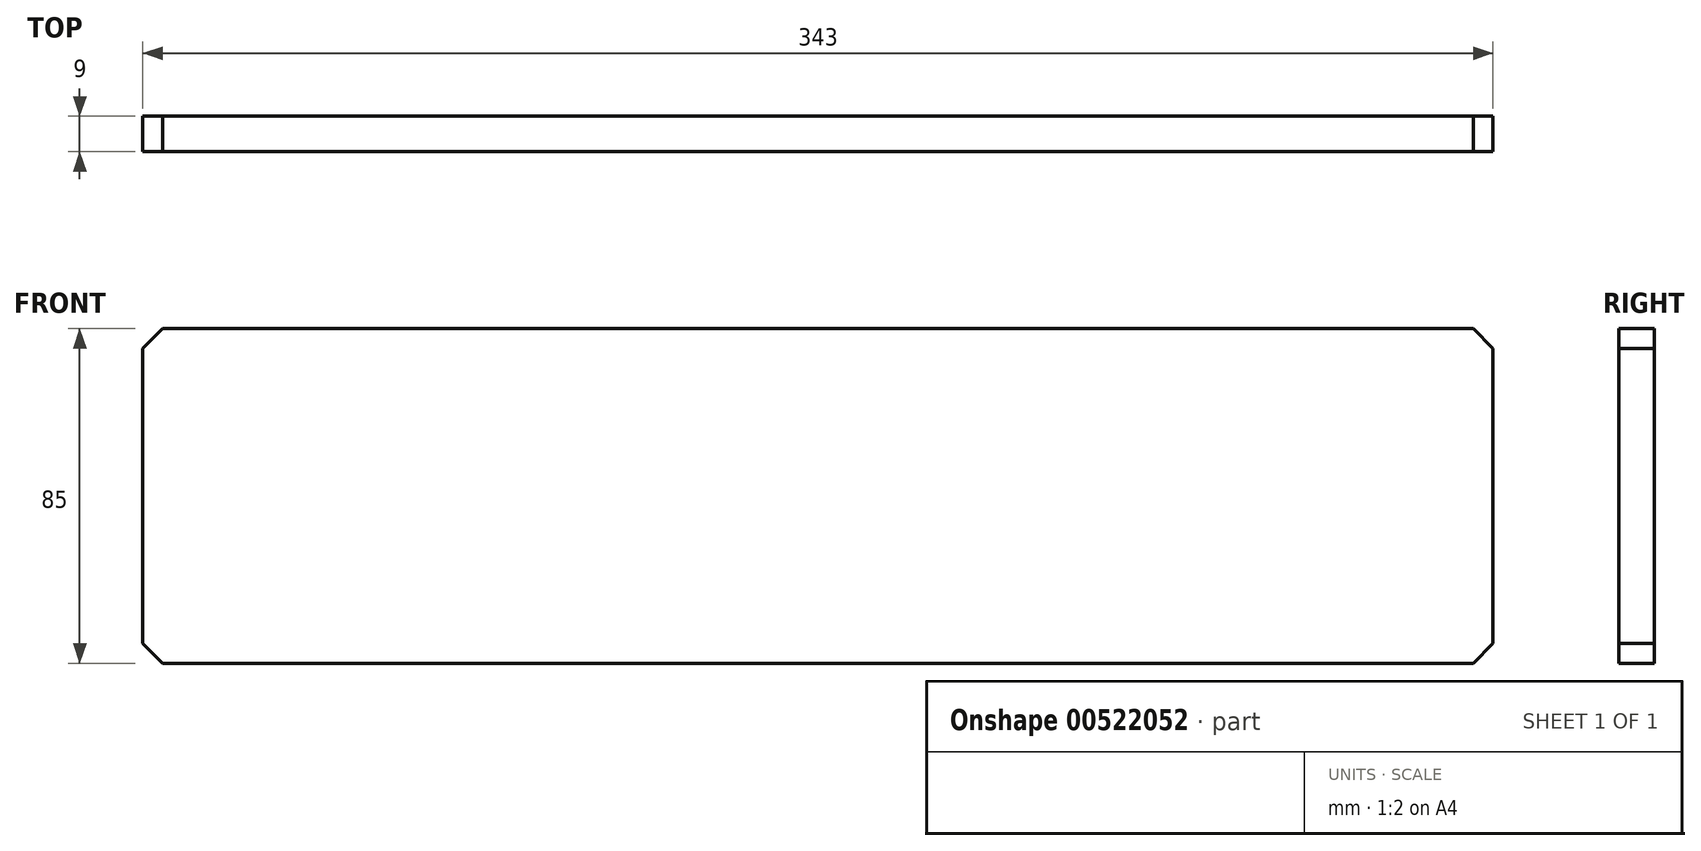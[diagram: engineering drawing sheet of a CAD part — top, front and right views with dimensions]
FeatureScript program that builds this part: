
annotation { "Feature Type Name" : "Feature", "Feature Type Description" : "" }
export const myFeature = defineFeature(function(context is Context, id is Id, definition is map)
    precondition{}
    {
        {
            var Q0;
            Q0=qCreatedBy(makeId("Front.planeOp"),FACE);
            var sketch = newSketch(context, id + "F0", { "sketchPlane" : qUnion([Q0])});
            skLineSegment(sketch, "E0.bottom", {"start": v(0, 0) * mm, "end": v(-343, 0) * mm});
            skLineSegment(sketch, "E0.top", {"start": v(0, 85) * mm, "end": v(-343, 85) * mm});
            skLineSegment(sketch, "E0.left", {"start": v(0, 0) * mm, "end": v(0, 85) * mm});
            skLineSegment(sketch, "E0.right", {"start": v(-343, 0) * mm, "end": v(-343, 85) * mm});
            skSolve(sketch);
        }
        {
            var Q0;
            Q0=makeQuery(id+"F0.imprint","IMPRINT",FACE,{"disambiguationData":[TD([[makeQuery(id+"F0.imprint","IMPRINT",EDGE,{"derivedFrom":sQuery(id+"F0.wireOp",EDGE,"E0.bottom")}),-1.0]])]});
            extrude(context, id + "F1", {"entities" : qUnion([Q0]), "depth" : 9 * mm, "offsetDistance" : 25 * mm});
        }
        {
            var Q0;
            Q0=makeQuery(id+"F1.opExtrude","SWEPT_EDGE",EDGE,{"disambiguationData":[OSD([sQuery(id+"F0.wireOp",EDGE,"E0.top"),sQuery(id+"F0.wireOp",EDGE,"E0.right")])]});
            var Q1;
            Q1=makeQuery(id+"F1.opExtrude","SWEPT_EDGE",EDGE,{"disambiguationData":[OSD([sQuery(id+"F0.wireOp",EDGE,"E0.top"),sQuery(id+"F0.wireOp",EDGE,"E0.left")])]});
            var Q2;
            Q2=makeQuery(id+"F1.opExtrude","SWEPT_EDGE",EDGE,{"disambiguationData":[OSD([sQuery(id+"F0.wireOp",EDGE,"E0.bottom"),sQuery(id+"F0.wireOp",EDGE,"E0.left")])]});
            var Q3;
            Q3=makeQuery(id+"F1.opExtrude","SWEPT_EDGE",EDGE,{"disambiguationData":[OSD([sQuery(id+"F0.wireOp",EDGE,"E0.bottom"),sQuery(id+"F0.wireOp",EDGE,"E0.right")])]});
            chamfer(context, id + "F2", {"entities" : qUnion([Q0, Q1, Q2, Q3]), "width" : 5 * mm, "tangentPropagation" : true});
        }
    });
